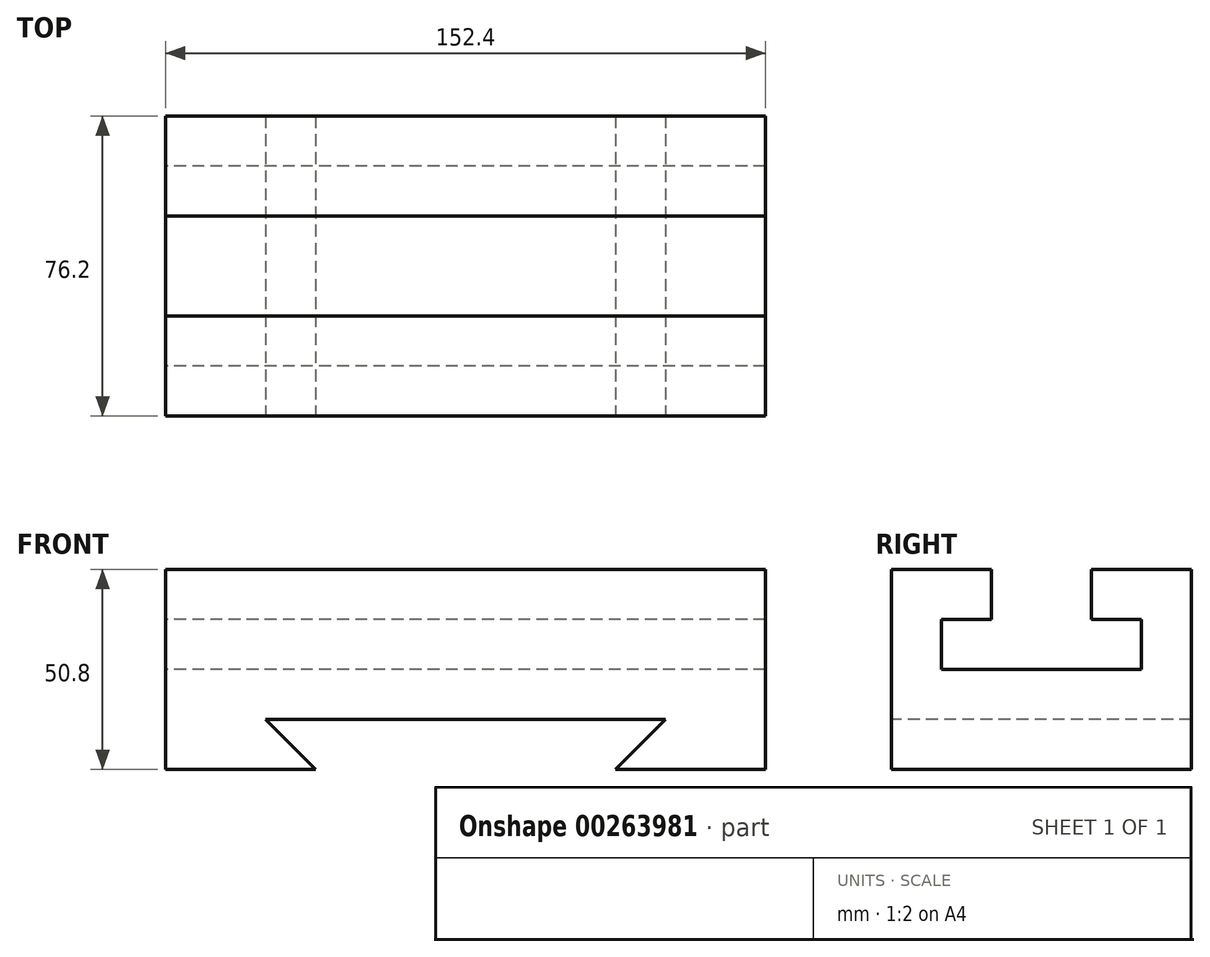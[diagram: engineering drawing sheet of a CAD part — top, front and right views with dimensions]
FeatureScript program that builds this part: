
annotation { "Feature Type Name" : "Feature", "Feature Type Description" : "" }
export const myFeature = defineFeature(function(context is Context, id is Id, definition is map)
    precondition{}
    {
        {
            var Q0;
            Q0=qCreatedBy(makeId("Right.planeOp"),FACE);
            var sketch = newSketch(context, id + "F0", { "sketchPlane" : qUnion([Q0])});
            skLineSegment(sketch, "E0", {"start": v(0, 0) * mm, "end": v(76.2, 0) * mm});
            skLineSegment(sketch, "E1", {"start": v(76.2, 0) * mm, "end": v(76.2, 50.8) * mm});
            skLineSegment(sketch, "E2", {"start": v(76.2, 50.8) * mm, "end": v(50.8, 50.8) * mm});
            skLineSegment(sketch, "E3", {"start": v(50.8, 50.8) * mm, "end": v(50.8, 38.1) * mm});
            skLineSegment(sketch, "E4", {"start": v(50.8, 38.1) * mm, "end": v(63.5, 38.1) * mm});
            skLineSegment(sketch, "E5", {"start": v(63.5, 38.1) * mm, "end": v(63.5, 25.4) * mm});
            skLineSegment(sketch, "E6", {"start": v(63.5, 25.4) * mm, "end": v(12.7, 25.4) * mm});
            skLineSegment(sketch, "E7", {"start": v(12.7, 25.4) * mm, "end": v(12.7, 38.1) * mm});
            skLineSegment(sketch, "E8", {"start": v(12.7, 38.1) * mm, "end": v(25.4, 38.1) * mm});
            skLineSegment(sketch, "E9", {"start": v(25.4, 38.1) * mm, "end": v(25.4, 50.8) * mm});
            skLineSegment(sketch, "E10", {"start": v(25.4, 50.8) * mm, "end": v(0, 50.8) * mm});
            skLineSegment(sketch, "E11", {"start": v(0, 50.8) * mm, "end": v(0, 0) * mm});
            skSolve(sketch);
        }
        {
            var Q0;
            Q0 = qSketchRegion(id + "F0", true);
            extrude(context, id + "F1", {"entities" : qUnion([Q0]), "depth" : 152.4 * mm});
        }
        {
            var Q0;
            Q0=makeQuery(id+"F1.opExtrude","SWEPT_FACE",FACE,{"disambiguationData":[OSD([sQuery(id+"F0.wireOp",EDGE,"E11")])]});
            var sketch = newSketch(context, id + "F2", { "sketchPlane" : qUnion([Q0])});
            skLineSegment(sketch, "E12", {"start": v(0, 0) * mm, "end": v(38.1, 0) * mm});
            skLineSegment(sketch, "E13", {"start": v(38.1, 0) * mm, "end": v(25.4, 12.7) * mm});
            skLineSegment(sketch, "E14", {"start": v(25.4, 12.7) * mm, "end": v(127, 12.7) * mm});
            skLineSegment(sketch, "E15", {"start": v(152.4, 0) * mm, "end": v(114.3, 0) * mm});
            skLineSegment(sketch, "E16", {"start": v(114.3, 0) * mm, "end": v(127, 12.7) * mm});
            skSolve(sketch);
        }
        {
            var Q0;
            Q0 = qSketchRegion(id + "F2", true);
            var Q1;
            {var subQ0=sQuery(id+"F2.wireOp",EDGE,"E13");Q1=makeQuery(id+"F2.imprint","IMPRINT",FACE,{"disambiguationData":[TD([[makeQuery(id+"F2.imprint","IMPRINT",EDGE,{"derivedFrom":subQ0}),-1.0]])]});}
            extrude(context, id + "F3", {"entities" : qUnion([Q0, Q1]), "operationType" : NewBodyOperationType.REMOVE, "oppositeDirection" : true, "depth" : 80.77 * mm});
        }
    });
